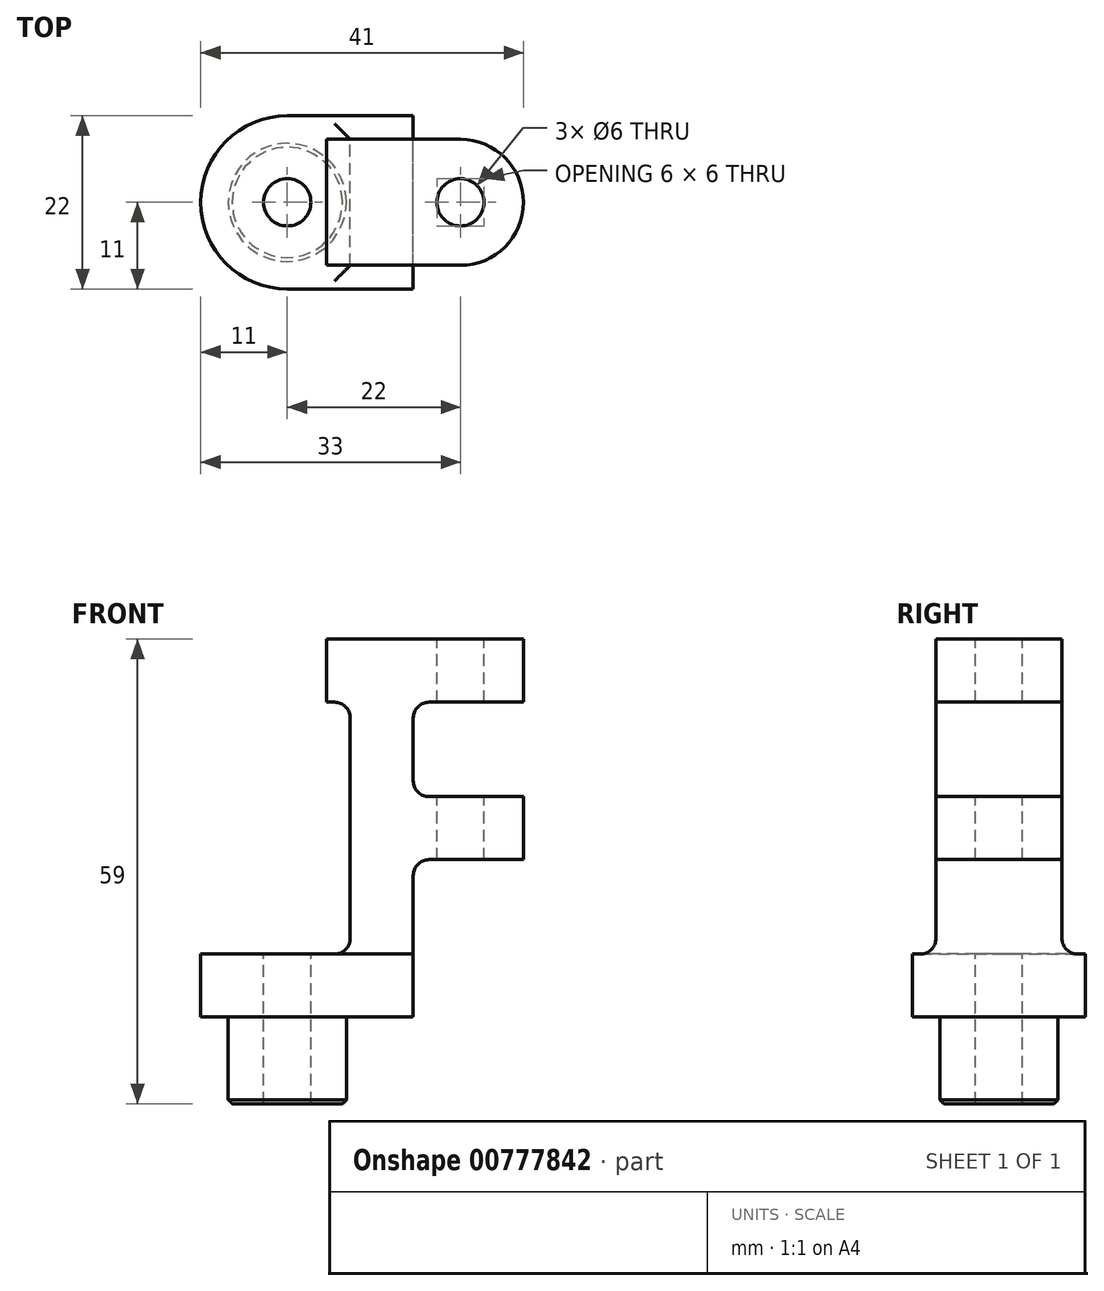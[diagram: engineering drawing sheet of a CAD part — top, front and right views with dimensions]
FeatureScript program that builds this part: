
annotation { "Feature Type Name" : "Feature", "Feature Type Description" : "" }
export const myFeature = defineFeature(function(context is Context, id is Id, definition is map)
    precondition{}
    {
        {
            var Q0;
            Q0=qCreatedBy(makeId("Front.planeOp"),FACE);
            var sketch = newSketch(context, id + "F0", { "sketchPlane" : qUnion([Q0])});
            skLineSegment(sketch, "E0", {"start": v(0, -11) * mm, "end": v(-15, -11) * mm});
            skLineSegment(sketch, "E1", {"start": v(-15, -11) * mm, "end": v(-15, 0) * mm});
            skLineSegment(sketch, "E2", {"start": v(-15, 0) * mm, "end": v(-18.5, 0) * mm});
            skLineSegment(sketch, "E3", {"start": v(-18.5, 0) * mm, "end": v(-18.5, 8) * mm});
            skLineSegment(sketch, "E4", {"start": v(-18.5, 8) * mm, "end": v(0.5, 8) * mm});
            skLineSegment(sketch, "E5", {"start": v(0.5, 8) * mm, "end": v(0.5, 40) * mm});
            skLineSegment(sketch, "E6", {"start": v(0.5, 40) * mm, "end": v(-2.5, 40) * mm});
            skLineSegment(sketch, "E7", {"start": v(-2.5, 40) * mm, "end": v(-2.5, 48) * mm});
            skLineSegment(sketch, "E8", {"start": v(-2.5, 48) * mm, "end": v(22.5, 48) * mm});
            skLineSegment(sketch, "E9", {"start": v(22.5, 48) * mm, "end": v(22.5, 40) * mm});
            skLineSegment(sketch, "E10", {"start": v(22.5, 40) * mm, "end": v(8.5, 40) * mm});
            skLineSegment(sketch, "E11", {"start": v(8.5, 40) * mm, "end": v(8.5, 28) * mm});
            skLineSegment(sketch, "E12", {"start": v(8.5, 28) * mm, "end": v(22.5, 28) * mm});
            skLineSegment(sketch, "E13", {"start": v(22.5, 28) * mm, "end": v(22.5, 20) * mm});
            skLineSegment(sketch, "E14", {"start": v(22.5, 20) * mm, "end": v(8.5, 20) * mm});
            skLineSegment(sketch, "E15", {"start": v(8.5, 20) * mm, "end": v(8.5, 0) * mm});
            skLineSegment(sketch, "E16", {"start": v(8.5, 0) * mm, "end": v(0, 0) * mm});
            skLineSegment(sketch, "E17", {"start": v(0, 0) * mm, "end": v(0, -11) * mm});
            skLineSegment(sketch, "E18", {"start": v(-7.5, -12.34) * mm, "end": v(-7.5, 9.3) * mm, "construction": true});
            skPoint(sketch, "E18.startSnap0", {"position": v(-7.5, -11) * mm});
            skSolve(sketch);
        }
        {
            var Q0;
            Q0=makeQuery(id+"F0.imprint","IMPRINT",FACE,{"disambiguationData":[TD([[makeQuery(id+"F0.imprint","IMPRINT",EDGE,{"derivedFrom":sQuery(id+"F0.wireOp",EDGE,"E0")}),-1.0]])]});
            extrude(context, id + "F1", {"entities" : qUnion([Q0]), "endBound" : BoundingType.SYMMETRIC, "depth" : 22 * mm, "offsetDistance" : 25 * mm});
        }
        {
            var Q0;
            Q0=qCreatedBy(makeId("Right.planeOp"),FACE);
            var sketch = newSketch(context, id + "F2", { "sketchPlane" : qUnion([Q0])});
            skLineSegment(sketch, "E19.bottom", {"start": v(-16, 53) * mm, "end": v(-8, 53) * mm});
            skLineSegment(sketch, "E19.top", {"start": v(-16, 8) * mm, "end": v(-8, 8) * mm});
            skLineSegment(sketch, "E19.left", {"start": v(-16, 53) * mm, "end": v(-16, 8) * mm});
            skLineSegment(sketch, "E19.right", {"start": v(-8, 53) * mm, "end": v(-8, 8) * mm});
            skLineSegment(sketch, "E20.MirrorCS", {"start": v(8, 53) * mm, "end": v(8, 8) * mm});
            skLineSegment(sketch, "E21.MirrorCS", {"start": v(16, 53) * mm, "end": v(8, 53) * mm});
            skLineSegment(sketch, "E22.MirrorCS", {"start": v(16, 53) * mm, "end": v(16, 8) * mm});
            skLineSegment(sketch, "E23.MirrorCS", {"start": v(16, 8) * mm, "end": v(8, 8) * mm});
            skLineSegment(sketch, "E24.bottom", {"start": v(-16, -15) * mm, "end": v(-7.5, -15) * mm});
            skLineSegment(sketch, "E24.top", {"start": v(-16, 0) * mm, "end": v(-7.5, 0) * mm});
            skLineSegment(sketch, "E24.left", {"start": v(-16, -15) * mm, "end": v(-16, 0) * mm});
            skLineSegment(sketch, "E24.right", {"start": v(-7.5, -15) * mm, "end": v(-7.5, 0) * mm});
            skLineSegment(sketch, "E25.MirrorCS", {"start": v(7.5, -15) * mm, "end": v(7.5, 0) * mm});
            skLineSegment(sketch, "E26.MirrorCS", {"start": v(16, -15) * mm, "end": v(7.5, -15) * mm});
            skLineSegment(sketch, "E27.MirrorCS", {"start": v(16, -15) * mm, "end": v(16, 0) * mm});
            skLineSegment(sketch, "E28.MirrorCS", {"start": v(16, 0) * mm, "end": v(7.5, 0) * mm});
            skSolve(sketch);
        }
        {
            var Q0;
            Q0 = qSketchRegion(id + "F2", true);
            extrude(context, id + "F3", {"entities" : qUnion([Q0]), "operationType" : NewBodyOperationType.REMOVE, "endBound" : BoundingType.SYMMETRIC, "oppositeDirection" : true, "depth" : 50 * mm, "offsetDistance" : 25 * mm});
        }
        {
            var Q0;
            Q0=makeQuery(id+"F3.boolean.opBoolean","INTERSECT",EDGE,{"derivedFrom":[makeQuery(id+"F1.opExtrude","SWEPT_FACE",FACE,{"disambiguationData":[OSD([sQuery(id+"F0.wireOp",EDGE,"E17")])]}),makeQuery(id+"F3.opExtrude","SWEPT_FACE",FACE,{"disambiguationData":[OSD([sQuery(id+"F2.wireOp",EDGE,"E24.right")])]})]});
            var Q1;
            Q1=makeQuery(id+"F3.boolean.opBoolean","INTERSECT",EDGE,{"derivedFrom":[makeQuery(id+"F1.opExtrude","SWEPT_FACE",FACE,{"disambiguationData":[OSD([sQuery(id+"F0.wireOp",EDGE,"E1")])]}),makeQuery(id+"F3.opExtrude","SWEPT_FACE",FACE,{"disambiguationData":[OSD([sQuery(id+"F2.wireOp",EDGE,"E24.right")])]})]});
            var Q2;
            Q2=makeQuery(id+"F3.boolean.opBoolean","INTERSECT",EDGE,{"derivedFrom":[makeQuery(id+"F1.opExtrude","SWEPT_FACE",FACE,{"disambiguationData":[OSD([sQuery(id+"F0.wireOp",EDGE,"E17")])]}),makeQuery(id+"F3.opExtrude","SWEPT_FACE",FACE,{"disambiguationData":[OSD([sQuery(id+"F2.wireOp",EDGE,"E25.MirrorCS")])]})]});
            var Q3;
            Q3=makeQuery(id+"F3.boolean.opBoolean","INTERSECT",EDGE,{"derivedFrom":[makeQuery(id+"F1.opExtrude","SWEPT_FACE",FACE,{"disambiguationData":[OSD([sQuery(id+"F0.wireOp",EDGE,"E1")])]}),makeQuery(id+"F3.opExtrude","SWEPT_FACE",FACE,{"disambiguationData":[OSD([sQuery(id+"F2.wireOp",EDGE,"E25.MirrorCS")])]})]});
            fillet(context, id + "F4", {"entities" : qUnion([Q0, Q1, Q2, Q3]), "radius" : 7.5 * mm, "tangentPropagation" : true, "allowEdgeOverflow" : false});
        }
        {
            var Q0;
            Q0=makeQuery(id+"F1.opExtrude","CAP_EDGE",EDGE,{"disambiguationData":[OSD([sQuery(id+"F0.wireOp",EDGE,"E3")])],"isStart":true});
            var Q1;
            Q1=makeQuery(id+"F1.opExtrude","CAP_EDGE",EDGE,{"disambiguationData":[OSD([sQuery(id+"F0.wireOp",EDGE,"E3")])],"isStart":false});
            fillet(context, id + "F5", {"entities" : qUnion([Q0, Q1]), "radius" : 11 * mm, "tangentPropagation" : true, "allowEdgeOverflow" : false});
        }
        {
            var Q0;
            Q0=makeQuery(id+"F3.boolean.opBoolean","INTERSECT",EDGE,{"derivedFrom":[makeQuery(id+"F1.opExtrude","SWEPT_FACE",FACE,{"disambiguationData":[OSD([sQuery(id+"F0.wireOp",EDGE,"E9")])]}),makeQuery(id+"F3.opExtrude","SWEPT_FACE",FACE,{"disambiguationData":[OSD([sQuery(id+"F2.wireOp",EDGE,"E20.MirrorCS")])]})]});
            var Q1;
            Q1=makeQuery(id+"F3.boolean.opBoolean","INTERSECT",EDGE,{"derivedFrom":[makeQuery(id+"F1.opExtrude","SWEPT_FACE",FACE,{"disambiguationData":[OSD([sQuery(id+"F0.wireOp",EDGE,"E13")])]}),makeQuery(id+"F3.opExtrude","SWEPT_FACE",FACE,{"disambiguationData":[OSD([sQuery(id+"F2.wireOp",EDGE,"E20.MirrorCS")])]})]});
            var Q2;
            Q2=makeQuery(id+"F3.boolean.opBoolean","INTERSECT",EDGE,{"derivedFrom":[makeQuery(id+"F1.opExtrude","SWEPT_FACE",FACE,{"disambiguationData":[OSD([sQuery(id+"F0.wireOp",EDGE,"E13")])]}),makeQuery(id+"F3.opExtrude","SWEPT_FACE",FACE,{"disambiguationData":[OSD([sQuery(id+"F2.wireOp",EDGE,"E19.right")])]})]});
            var Q3;
            Q3=makeQuery(id+"F3.boolean.opBoolean","INTERSECT",EDGE,{"derivedFrom":[makeQuery(id+"F1.opExtrude","SWEPT_FACE",FACE,{"disambiguationData":[OSD([sQuery(id+"F0.wireOp",EDGE,"E9")])]}),makeQuery(id+"F3.opExtrude","SWEPT_FACE",FACE,{"disambiguationData":[OSD([sQuery(id+"F2.wireOp",EDGE,"E19.right")])]})]});
            fillet(context, id + "F6", {"entities" : qUnion([Q0, Q1, Q2, Q3]), "radius" : 8 * mm, "tangentPropagation" : true, "allowEdgeOverflow" : false});
        }
        {
            var Q0;
            Q0=makeQuery(id+"F1.opExtrude","SWEPT_EDGE",EDGE,{"disambiguationData":[OSD([sQuery(id+"F0.wireOp",EDGE,"E11"),sQuery(id+"F0.wireOp",EDGE,"E12")])]});
            var Q1;
            Q1=makeQuery(id+"F1.opExtrude","SWEPT_EDGE",EDGE,{"disambiguationData":[OSD([sQuery(id+"F0.wireOp",EDGE,"E10"),sQuery(id+"F0.wireOp",EDGE,"E11")])]});
            var Q2;
            Q2=makeQuery(id+"F1.opExtrude","SWEPT_EDGE",EDGE,{"disambiguationData":[OSD([sQuery(id+"F0.wireOp",EDGE,"E5"),sQuery(id+"F0.wireOp",EDGE,"E6")])]});
            var Q3;
            Q3=makeQuery(id+"F1.opExtrude","SWEPT_EDGE",EDGE,{"disambiguationData":[OSD([sQuery(id+"F0.wireOp",EDGE,"E4"),sQuery(id+"F0.wireOp",EDGE,"E5")])]});
            var Q4;
            Q4=makeQuery(id+"F3.boolean.opBoolean","COPY",EDGE,{"derivedFrom":makeQuery(id+"F3.opExtrude","SWEPT_EDGE",EDGE,{"disambiguationData":[OSD([sQuery(id+"F2.wireOp",EDGE,"E19.top"),sQuery(id+"F2.wireOp",EDGE,"E19.right")])]})});
            var Q5;
            Q5=makeQuery(id+"F3.boolean.opBoolean","COPY",EDGE,{"derivedFrom":makeQuery(id+"F3.opExtrude","SWEPT_EDGE",EDGE,{"disambiguationData":[OSD([sQuery(id+"F2.wireOp",EDGE,"E20.MirrorCS"),sQuery(id+"F2.wireOp",EDGE,"E23.MirrorCS")])]})});
            var Q6;
            Q6=makeQuery(id+"F1.opExtrude","SWEPT_EDGE",EDGE,{"disambiguationData":[OSD([sQuery(id+"F0.wireOp",EDGE,"E14"),sQuery(id+"F0.wireOp",EDGE,"E15")])]});
            fillet(context, id + "F7", {"entities" : qUnion([Q0, Q1, Q2, Q3, Q4, Q5, Q6]), "radius" : 2 * mm, "tangentPropagation" : true, "allowEdgeOverflow" : false});
        }
        {
            var Q0;
            Q0=makeQuery(id+"F3.boolean.opBoolean","MERGE",FACE,{"derivedFrom":[makeQuery(id+"F1.opExtrude","SWEPT_FACE",FACE,{"disambiguationData":[OSD([sQuery(id+"F0.wireOp",EDGE,"E4")])]}),makeQuery(id+"F3.opExtrude","SWEPT_FACE",FACE,{"disambiguationData":[OSD([sQuery(id+"F2.wireOp",EDGE,"E19.top")])]}),makeQuery(id+"F3.opExtrude","SWEPT_FACE",FACE,{"disambiguationData":[OSD([sQuery(id+"F2.wireOp",EDGE,"E23.MirrorCS")])]})]});
            var sketch = newSketch(context, id + "F8", { "sketchPlane" : qUnion([Q0])});
            skCircle(sketch, "E29", {"center": v(-7.5, 0) * mm, "radius": 3 * mm});
            skSolve(sketch);
        }
        {
            var Q0;
            Q0 = qSketchRegion(id + "F8", true);
            extrude(context, id + "F9", {"entities" : qUnion([Q0]), "operationType" : NewBodyOperationType.REMOVE, "oppositeDirection" : true, "depth" : 19 * mm, "offsetDistance" : 25 * mm});
        }
        {
            var Q0;
            Q0=makeQuery(id+"F1.opExtrude","SWEPT_FACE",FACE,{"disambiguationData":[OSD([sQuery(id+"F0.wireOp",EDGE,"E8")])]});
            var sketch = newSketch(context, id + "F10", { "sketchPlane" : qUnion([Q0])});
            skCircle(sketch, "E30", {"center": v(14.5, 0) * mm, "radius": 3 * mm});
            skSolve(sketch);
        }
        {
            var Q0;
            Q0 = qSketchRegion(id + "F10", true);
            extrude(context, id + "F11", {"entities" : qUnion([Q0]), "operationType" : NewBodyOperationType.REMOVE, "oppositeDirection" : true, "depth" : 35 * mm, "offsetDistance" : 25 * mm});
        }
        {
            var Q0;
            Q0=makeQuery(id+"F4.opFillet","BLEND_EDGE",EDGE,{"blendedFrom":[makeQuery(id+"F3.boolean.opBoolean","INTERSECT",EDGE,{"derivedFrom":[makeQuery(id+"F1.opExtrude","SWEPT_FACE",FACE,{"disambiguationData":[OSD([sQuery(id+"F0.wireOp",EDGE,"E1")])]}),makeQuery(id+"F3.opExtrude","SWEPT_FACE",FACE,{"disambiguationData":[OSD([sQuery(id+"F2.wireOp",EDGE,"E24.right")])]})]}),makeQuery(id+"F1.opExtrude","SWEPT_FACE",FACE,{"disambiguationData":[OSD([sQuery(id+"F0.wireOp",EDGE,"E0")])]})],"blendedInto":[makeQuery(id+"F1.opExtrude","SWEPT_FACE",FACE,{"disambiguationData":[OSD([sQuery(id+"F0.wireOp",EDGE,"E0")])]})]});
            chamfer(context, id + "F12", {"entities" : qUnion([Q0]), "width" : 0.5 * mm, "tangentPropagation" : true});
        }
    });
